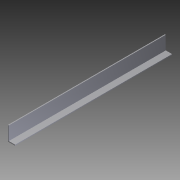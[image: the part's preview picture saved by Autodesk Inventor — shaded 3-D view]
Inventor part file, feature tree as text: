
AUTODESK INVENTOR PART (.ipt)
format: ipt  version: 2012 (Build 160160000, 160)  size: 72,192 bytes
history: native  units: in
note: dims shown in document units (in); Inventor stores cm internally (conversion verified against a paired STEP export)
features: extrude x1, sketch x1
ambient origin geometry x8: Origin, YZ Plane, XZ Plane, XY Plane, X Axis, Y Axis, Z Axis, Center Point
bodies: Solid1 (feature_tree)
feature tree (2):
  extrude  "Extrusion1"  Depth=1.0in
  sketch  "Sketch1"  dims[d0=2.0in d1=1.0in d2=0.125in d3=0.125in d4=21.75in d5=0.0in]
